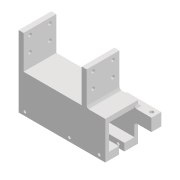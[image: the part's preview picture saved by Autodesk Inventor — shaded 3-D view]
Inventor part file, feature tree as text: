
AUTODESK INVENTOR PART (.ipt)
format: ipt  version: 2022 (Build 260153000, 153)  size: 230,912 bytes
history: native  units: mm
features: extrude x7, sketch x7, projected_geometry x5, fillet x2
ambient origin geometry x8: Origin, YZ Plane, XZ Plane, XY Plane, X Axis, Y Axis, Z Axis, Center Point
bodies: Solid1 (feature_tree)
feature tree (21):
  extrude  "Extrusion1"  Depth=20.4mm
  extrude  "Extrusion3"  Depth=54.8mm TaperAngle=0.0deg
  extrude  "Extrusion8"  Depth=3.0mm
  extrude  "Extrusion9"  Depth=8.0mm
  fillet  "Fillet3"  Radius=8.0mm
  extrude  "Extrusion10"  Depth=10.0mm
  extrude  "Extrusion11"  TaperAngle=0.0deg  [1 undecoded]
  extrude  "Extrusion12"  Depth=3.0mm TaperAngle=0.0deg
  fillet  "Fillet4"  Radius=3.0mm
  sketch  "Sketch2"  dims[d5=20.4mm d6=20.4mm]
  sketch  "Sketch4"  dims[d8=6.0mm d9=54.8mm d10=0.0mm]
  projected_geometry  "Projected Loop2"
  sketch  "Sketch10"  dims[d22=4.0mm d23=3.0mm]
  projected_geometry  "Projected Loop8"
  sketch  "Sketch11"  dims[d24=3.0mm d27=8.0mm d28=8.0mm]
  projected_geometry  "Projected Loop9"
  projected_geometry  "Projected Loop10"
  sketch  "Sketch12"  dims[d29=10.0mm d30=11.25mm]
  projected_geometry  "Projected Loop11"
  sketch  "Sketch13"  dims[d31=40.0mm d32=0.0mm]
  sketch  "Sketch14"  dims[d33=5.0mm d34=0.0mm d49=3.0mm d50=0.0mm d55=3.0mm d56=4.0mm d57=4.0mm d58=10.0mm d59=0.0mm d61=15.0mm d62=0.0mm d63=2.0mm d64=2.2mm d65=5.0mm d66=3.0mm d67=2.2mm d68=2.2mm d69=5.0mm d70=3.0mm d71=29.0mm d72=3.0mm d73=100.0mm d74=0.0mm d75=4.0mm d76=4.0mm d77=46.8mm d78=27.0mm d79=0.0mm d80=2.6mm d81=11.0mm d82=2.6mm d83=23.0mm d86=2.6mm d87=2.6mm d88=11.0mm d89=23.0mm d92=100.0mm d93=0.0mm d94=2.0mm d95=16.0mm d96=16.0mm d97=5.2mm d98=5.2mm]
note: 1 required parameter value undecoded (feature->parameter linkage not recoverable at this tier; creation-order binding heuristic only, values carry confidence <= 0.55)
